# Revit family: Krowne_16-302L_DeckMount_Faucet
name_source: partatom
category: Plumbing Fixtures
revit_build: Autodesk Revit 2018 (Build: 20170223_1515(x64)
units: mm (PartAtom-declared; Revit-internal decimal feet)

## family parameters
Always vertical = Yes
Cut with Voids When Loaded = No
OmniClass Number = 23.40.40.00
OmniClass Title = Food Service Equipment and Furnishings
Part Type = Normal
Room Calculation Point = No
Round Connector Dimension = Use Diameter
Shared = No
Work Plane-Based = No

## types (1)
- 16-302L
    Assembly Code = E1090300
    Cold Water Connection Height = 0"
    Cold Water Flow = 2 GPM
    Cold Water Size = 1"
    Depth = 7"
    Description = Single Hole Deck Mount Pantry Faucet with 8-1/2" Wide Gooseneck Spout
    Foodservice Equipment Identifier = Yes
    Height = 13 7/8"
    Hot Water Connection Height = 0"
    Hot Water Flow = 2 GPM
    Hot Water RI Height = 0"
    Hot Water Size = 1"
    Hot Water Temperature = 100 °F
    Manufacturer = Krowne Metal
    Model = 16-302L
    URL = https://krowne.com
    Weight in Pounds = 5
    Width = 7"

## geometry (parser evidence)
native form markers: Blend x4, Sweep x2
no freeform markers — native parametric forms only
